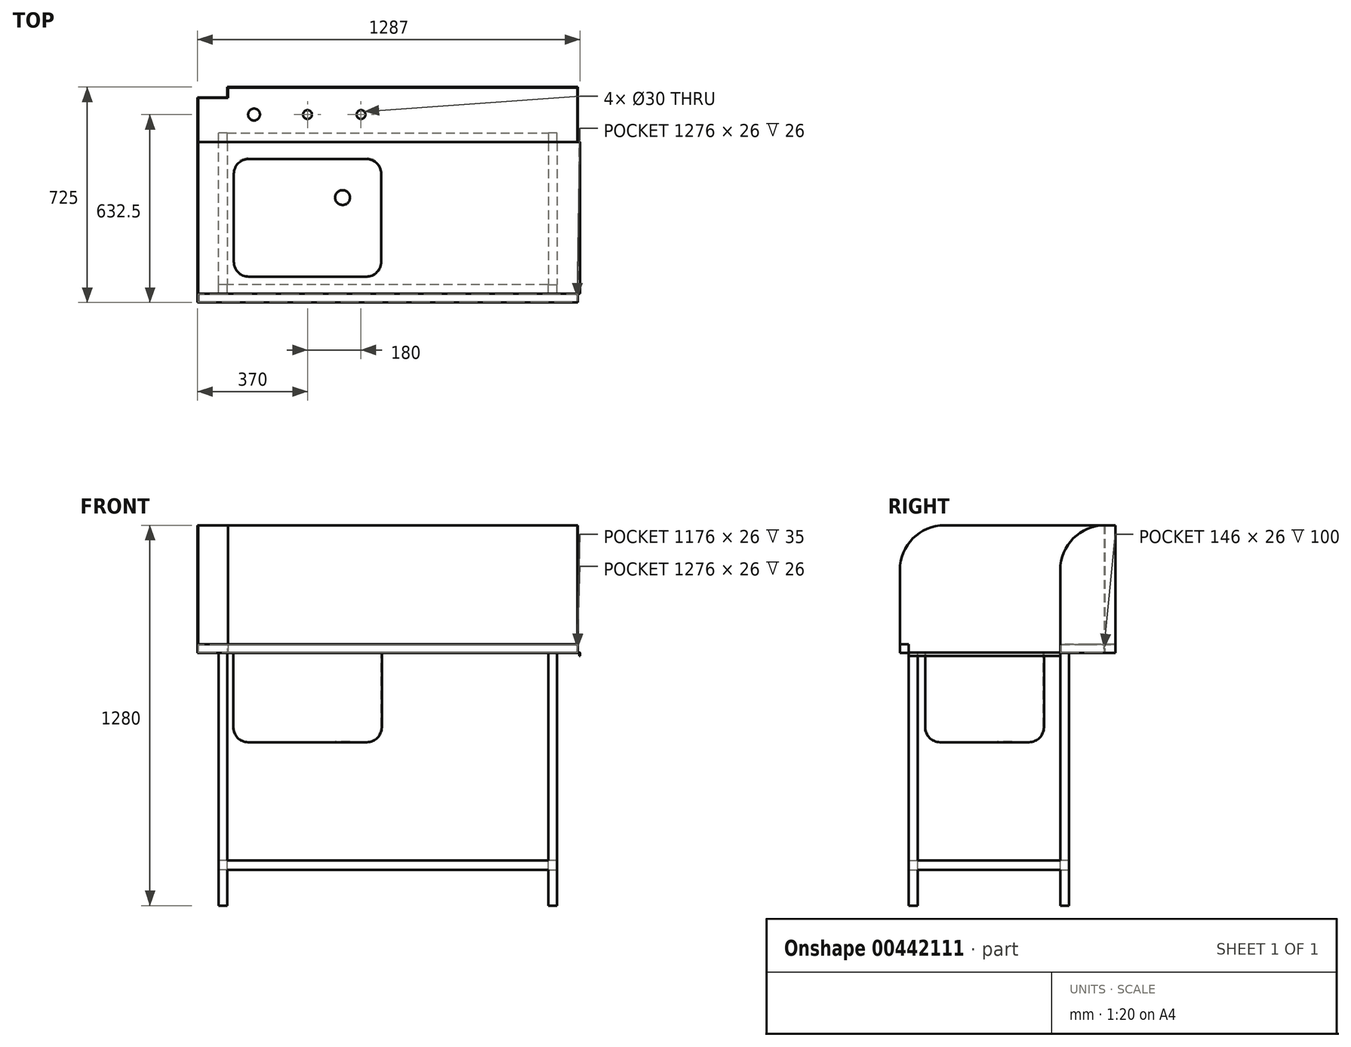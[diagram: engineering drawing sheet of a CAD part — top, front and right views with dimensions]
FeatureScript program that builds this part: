
annotation { "Feature Type Name" : "Feature", "Feature Type Description" : "" }
export const myFeature = defineFeature(function(context is Context, id is Id, definition is map)
    precondition{}
    {
        {
            var Q0;
            Q0=qCreatedBy(makeId("Top.planeOp"),FACE);
            var sketch = newSketch(context, id + "F0", { "sketchPlane" : qUnion([Q0])});
            skLineSegment(sketch, "E0", {"start": v(0, 0) * mm, "end": v(1280, 0) * mm});
            skLineSegment(sketch, "E1", {"start": v(1280, 0) * mm, "end": v(1280, 725) * mm});
            skLineSegment(sketch, "E2", {"start": v(1280, 725) * mm, "end": v(100, 725) * mm});
            skLineSegment(sketch, "E3", {"start": v(100, 725) * mm, "end": v(100, 690) * mm});
            skLineSegment(sketch, "E4", {"start": v(100, 690) * mm, "end": v(0, 690) * mm});
            skLineSegment(sketch, "E5", {"start": v(0, 690) * mm, "end": v(0, 0) * mm});
            skSolve(sketch);
        }
        {
            var Q0;
            Q0 = qSketchRegion(id + "F0", true);
            extrude(context, id + "F1", {"entities" : qUnion([Q0]), "depth" : 30 * mm});
        }
        {
            var Q0;
            Q0=makeQuery(id+"F1.opExtrude","CAP_FACE",FACE,{"disambiguationData":[OSD([sQuery(id+"F0.wireOp",EDGE,"E0"),sQuery(id+"F0.wireOp",EDGE,"E1"),sQuery(id+"F0.wireOp",EDGE,"E2"),sQuery(id+"F0.wireOp",EDGE,"E3"),sQuery(id+"F0.wireOp",EDGE,"E4"),sQuery(id+"F0.wireOp",EDGE,"E5")])],"isStart":false});
            var sketch = newSketch(context, id + "F2", { "sketchPlane" : qUnion([Q0])});
            skLineSegment(sketch, "E6.bottom", {"start": v(2, 30) * mm, "end": v(1280, 30) * mm});
            skLineSegment(sketch, "E6.top", {"start": v(2, 540) * mm, "end": v(1280, 540) * mm});
            skLineSegment(sketch, "E6.left", {"start": v(2, 30) * mm, "end": v(2, 540) * mm});
            skLineSegment(sketch, "E6.right", {"start": v(1280, 30) * mm, "end": v(1280, 540) * mm});
            skSolve(sketch);
        }
        {
            var Q0;
            Q0 = qSketchRegion(id + "F2", true);
            extrude(context, id + "F3", {"entities" : qUnion([Q0]), "operationType" : NewBodyOperationType.REMOVE, "oppositeDirection" : true, "depth" : 28 * mm});
        }
        {
            var Q0;
            Q0=makeQuery(id+"F1.opExtrude","CAP_FACE",FACE,{"disambiguationData":[OSD([sQuery(id+"F0.wireOp",EDGE,"E0"),sQuery(id+"F0.wireOp",EDGE,"E1"),sQuery(id+"F0.wireOp",EDGE,"E2"),sQuery(id+"F0.wireOp",EDGE,"E3"),sQuery(id+"F0.wireOp",EDGE,"E4"),sQuery(id+"F0.wireOp",EDGE,"E5")])],"isStart":true});
            var sketch = newSketch(context, id + "F4", { "sketchPlane" : qUnion([Q0])});
            skLineSegment(sketch, "E7.bottom", {"start": v(120, -85) * mm, "end": v(620, -85) * mm});
            skLineSegment(sketch, "E7.top", {"start": v(120, -485) * mm, "end": v(620, -485) * mm});
            skLineSegment(sketch, "E7.left", {"start": v(120, -85) * mm, "end": v(120, -485) * mm});
            skLineSegment(sketch, "E7.right", {"start": v(620, -85) * mm, "end": v(620, -485) * mm});
            skSolve(sketch);
        }
        {
            var Q0;
            Q0 = qSketchRegion(id + "F4", true);
            extrude(context, id + "F5", {"entities" : qUnion([Q0]), "operationType" : NewBodyOperationType.ADD, "depth" : 300 * mm});
        }
        {
            var Q0;
            Q0=makeQuery(id+"F3.boolean.opBoolean","COPY",FACE,{"derivedFrom":makeQuery(id+"F3.opExtrude","CAP_FACE",FACE,{"disambiguationData":[OSD([sQuery(id+"F2.wireOp",EDGE,"E6.bottom"),sQuery(id+"F2.wireOp",EDGE,"E6.top"),sQuery(id+"F2.wireOp",EDGE,"E6.left"),sQuery(id+"F2.wireOp",EDGE,"E6.right")])],"isStart":false})});
            shell(context, id + "F6", {"entities" : qUnion([Q0]), "thickness" : 2 * mm});
        }
        {
            var Q0;
            Q0=makeQuery(id+"F6.opShell","OFFSET_EDGE",EDGE,{"disambiguationData":[OSD([sQuery(id+"F4.wireOp",EDGE,"E7.top"),sQuery(id+"F4.wireOp",EDGE,"E7.left")])]});
            var Q1;
            Q1=makeQuery(id+"F6.opShell","OFFSET_EDGE",EDGE,{"disambiguationData":[OSD([sQuery(id+"F4.wireOp",EDGE,"E7.top"),sQuery(id+"F4.wireOp",EDGE,"E7.right")])]});
            var Q2;
            Q2=makeQuery(id+"F6.opShell","OFFSET_EDGE",EDGE,{"disambiguationData":[OSD([sQuery(id+"F4.wireOp",EDGE,"E7.bottom"),sQuery(id+"F4.wireOp",EDGE,"E7.left")])]});
            var Q3;
            Q3=makeQuery(id+"F6.opShell","OFFSET_EDGE",EDGE,{"disambiguationData":[OSD([sQuery(id+"F4.wireOp",EDGE,"E7.bottom"),sQuery(id+"F4.wireOp",EDGE,"E7.right")])]});
            var Q4;
            {var subQ0=sQuery(id+"F4.wireOp",EDGE,"E7.right");Q4=makeQuery(id+"F6.opShell","OFFSET_EDGE",EDGE,{"disambiguationData":[OSD([subQ0]),TDD([makeQuery(id+"F5.opExtrude","CAP_EDGE",EDGE,{"disambiguationData":[OSD([subQ0])],"isStart":false})])]});}
            var Q5;
            {var subQ0=sQuery(id+"F4.wireOp",EDGE,"E7.top");Q5=makeQuery(id+"F6.opShell","OFFSET_EDGE",EDGE,{"disambiguationData":[OSD([subQ0]),TDD([makeQuery(id+"F5.opExtrude","CAP_EDGE",EDGE,{"disambiguationData":[OSD([subQ0])],"isStart":false})])]});}
            var Q6;
            {var subQ0=sQuery(id+"F4.wireOp",EDGE,"E7.left");Q6=makeQuery(id+"F6.opShell","OFFSET_EDGE",EDGE,{"disambiguationData":[OSD([subQ0]),TDD([makeQuery(id+"F5.opExtrude","CAP_EDGE",EDGE,{"disambiguationData":[OSD([subQ0])],"isStart":false})])]});}
            var Q7;
            {var subQ0=sQuery(id+"F4.wireOp",EDGE,"E7.bottom");Q7=makeQuery(id+"F6.opShell","OFFSET_EDGE",EDGE,{"disambiguationData":[OSD([subQ0]),TDD([makeQuery(id+"F5.opExtrude","CAP_EDGE",EDGE,{"disambiguationData":[OSD([subQ0])],"isStart":false})])]});}
            var Q8;
            Q8=makeQuery(id+"F5.opExtrude","SWEPT_EDGE",EDGE,{"disambiguationData":[OSD([sQuery(id+"F4.wireOp",EDGE,"E7.bottom"),sQuery(id+"F4.wireOp",EDGE,"E7.left")])]});
            var Q9;
            Q9=makeQuery(id+"F5.opExtrude","CAP_EDGE",EDGE,{"disambiguationData":[OSD([sQuery(id+"F4.wireOp",EDGE,"E7.bottom")])],"isStart":false});
            var Q10;
            Q10=makeQuery(id+"F5.opExtrude","SWEPT_EDGE",EDGE,{"disambiguationData":[OSD([sQuery(id+"F4.wireOp",EDGE,"E7.bottom"),sQuery(id+"F4.wireOp",EDGE,"E7.right")])]});
            var Q11;
            Q11=makeQuery(id+"F5.opExtrude","CAP_EDGE",EDGE,{"disambiguationData":[OSD([sQuery(id+"F4.wireOp",EDGE,"E7.right")])],"isStart":false});
            var Q12;
            Q12=makeQuery(id+"F5.opExtrude","SWEPT_EDGE",EDGE,{"disambiguationData":[OSD([sQuery(id+"F4.wireOp",EDGE,"E7.top"),sQuery(id+"F4.wireOp",EDGE,"E7.right")])]});
            var Q13;
            Q13=makeQuery(id+"F5.opExtrude","CAP_EDGE",EDGE,{"disambiguationData":[OSD([sQuery(id+"F4.wireOp",EDGE,"E7.top")])],"isStart":false});
            var Q14;
            Q14=makeQuery(id+"F5.opExtrude","SWEPT_EDGE",EDGE,{"disambiguationData":[OSD([sQuery(id+"F4.wireOp",EDGE,"E7.top"),sQuery(id+"F4.wireOp",EDGE,"E7.left")])]});
            var Q15;
            Q15=makeQuery(id+"F5.opExtrude","CAP_EDGE",EDGE,{"disambiguationData":[OSD([sQuery(id+"F4.wireOp",EDGE,"E7.left")])],"isStart":false});
            fillet(context, id + "F7", {"entities" : qUnion([Q0, Q1, Q2, Q3, Q4, Q5, Q6, Q7, Q8, Q9, Q10, Q11, Q12, Q13, Q14, Q15]), "radius" : 50 * mm, "tangentPropagation" : true, "allowEdgeOverflow" : false});
        }
        {
            var Q0;
            Q0=makeQuery(id+"F6.opShell","OFFSET_FACE",FACE,{"disambiguationData":[OSD([sQuery(id+"F4.wireOp",EDGE,"E7.bottom"),sQuery(id+"F4.wireOp",EDGE,"E7.top"),sQuery(id+"F4.wireOp",EDGE,"E7.left"),sQuery(id+"F4.wireOp",EDGE,"E7.right")])]});
            var sketch = newSketch(context, id + "F8", { "sketchPlane" : qUnion([Q0])});
            skCircle(sketch, "E8", {"center": v(488, 353) * mm, "radius": 25 * mm});
            skSolve(sketch);
        }
        {
            var Q0;
            Q0 = qSketchRegion(id + "F8", true);
            extrude(context, id + "F9", {"entities" : qUnion([Q0]), "operationType" : NewBodyOperationType.REMOVE, "endBound" : BoundingType.UP_TO_NEXT, "oppositeDirection" : true, "depth" : 25 * mm});
        }
        {
            var Q0;
            Q0=makeQuery(id+"F1.opExtrude","CAP_FACE",FACE,{"disambiguationData":[OSD([sQuery(id+"F0.wireOp",EDGE,"E0"),sQuery(id+"F0.wireOp",EDGE,"E1"),sQuery(id+"F0.wireOp",EDGE,"E2"),sQuery(id+"F0.wireOp",EDGE,"E3"),sQuery(id+"F0.wireOp",EDGE,"E4"),sQuery(id+"F0.wireOp",EDGE,"E5")])],"isStart":false});
            var sketch = newSketch(context, id + "F10", { "sketchPlane" : qUnion([Q0])});
            skCircle(sketch, "E9", {"center": v(550, 632.5) * mm, "radius": 15 * mm});
            skCircle(sketch, "E10", {"center": v(370, 632.5) * mm, "radius": 15 * mm});
            skCircle(sketch, "E11", {"center": v(190, 632.5) * mm, "radius": 20 * mm});
            skSolve(sketch);
        }
        {
            var Q0;
            Q0 = qSketchRegion(id + "F10", true);
            var Q1;
            Q1=makeQuery(id+"F1.opExtrude","CAP_FACE",FACE,{"disambiguationData":[OSD([sQuery(id+"F0.wireOp",EDGE,"E0"),sQuery(id+"F0.wireOp",EDGE,"E1"),sQuery(id+"F0.wireOp",EDGE,"E2"),sQuery(id+"F0.wireOp",EDGE,"E3"),sQuery(id+"F0.wireOp",EDGE,"E4"),sQuery(id+"F0.wireOp",EDGE,"E5")])],"isStart":true});
            extrude(context, id + "F11", {"entities" : qUnion([Q0]), "operationType" : NewBodyOperationType.REMOVE, "endBound" : BoundingType.UP_TO_SURFACE, "oppositeDirection" : true, "endBoundEntityFace" : qUnion([Q1]), "depth" : 25 * mm});
        }
        {
            var Q0;
            Q0=makeQuery(id+"F1.opExtrude","SWEPT_FACE",FACE,{"disambiguationData":[OSD([sQuery(id+"F0.wireOp",EDGE,"E1")])]});
            var sketch = newSketch(context, id + "F12", { "sketchPlane" : qUnion([Q0])});
            skLineSegment(sketch, "E12.bottom", {"start": v(30, 2) * mm, "end": v(540, 2) * mm});
            skLineSegment(sketch, "E12.top", {"start": v(30, 0) * mm, "end": v(540, 0) * mm});
            skLineSegment(sketch, "E12.left", {"start": v(30, 2) * mm, "end": v(30, 0) * mm});
            skLineSegment(sketch, "E12.right", {"start": v(540, 2) * mm, "end": v(540, 0) * mm});
            skSolve(sketch);
        }
        {
            var Q0;
            Q0 = qSketchRegion(id + "F12", true);
            extrude(context, id + "F13", {"entities" : qUnion([Q0]), "operationType" : NewBodyOperationType.ADD, "depth" : 5 * mm});
        }
        {
            var Q0;
            Q0=makeQuery(id+"F13.opExtrude","CAP_FACE",FACE,{"disambiguationData":[OSD([sQuery(id+"F12.wireOp",EDGE,"E12.bottom"),sQuery(id+"F12.wireOp",EDGE,"E12.top"),sQuery(id+"F12.wireOp",EDGE,"E12.left"),sQuery(id+"F12.wireOp",EDGE,"E12.right")])],"isStart":false});
            var sketch = newSketch(context, id + "F14", { "sketchPlane" : qUnion([Q0])});
            skSolve(sketch);
        }
        {
            var Q0;
            Q0=makeQuery(id+"F14.imprint","IMPRINT",FACE,{"disambiguationData":[TD([[makeQuery(id+"F14.imprint","IMPRINT",EDGE,{"derivedFrom":makeQuery(id+"F13.opExtrude","CAP_EDGE",EDGE,{"disambiguationData":[OSD([sQuery(id+"F12.wireOp",EDGE,"E12.bottom")])],"isStart":false})}),-1.0]])]});
            var Q1;
            Q1=makeQuery(id+"F13.opExtrude","CAP_EDGE",EDGE,{"disambiguationData":[OSD([sQuery(id+"F12.wireOp",EDGE,"E12.top")])],"isStart":false});
            revolve(context, id + "F15", {"operationType" : NewBodyOperationType.ADD, "entities" : qUnion([Q0]), "axis" : qUnion([Q1]), "revolveType" : RevolveType.ONE_DIRECTION, "angle" : 90 * degree});
        }
        {
            var Q0;
            {var subQ0=sQuery(id+"F12.wireOp",EDGE,"E12.top");Q0=makeQuery(id+"F15.boolean.opBoolean","MERGE",FACE,{"derivedFrom":[makeQuery(id+"F13.boolean.opBoolean","MERGE",FACE,{"derivedFrom":[makeQuery(id+"F1.opExtrude","CAP_FACE",FACE,{"disambiguationData":[OSD([sQuery(id+"F0.wireOp",EDGE,"E0"),sQuery(id+"F0.wireOp",EDGE,"E1"),sQuery(id+"F0.wireOp",EDGE,"E2"),sQuery(id+"F0.wireOp",EDGE,"E3"),sQuery(id+"F0.wireOp",EDGE,"E4"),sQuery(id+"F0.wireOp",EDGE,"E5")])],"isStart":true}),makeQuery(id+"F13.opExtrude","SWEPT_FACE",FACE,{"disambiguationData":[OSD([subQ0])]})]}),makeQuery(id+"F15.opRevolve","CAP_FACE",FACE,{"disambiguationData":[OSD([sQuery(id+"F12.wireOp",EDGE,"E12.bottom"),subQ0,sQuery(id+"F12.wireOp",EDGE,"E12.left"),sQuery(id+"F12.wireOp",EDGE,"E12.right")])],"isStart":false})]});}
            var sketch = newSketch(context, id + "F16", { "sketchPlane" : qUnion([Q0])});
            skLineSegment(sketch, "E13.bottom", {"start": v(1287, -30) * mm, "end": v(1285, -30) * mm});
            skLineSegment(sketch, "E13.top", {"start": v(1287, -540) * mm, "end": v(1285, -540) * mm});
            skLineSegment(sketch, "E13.left", {"start": v(1287, -30) * mm, "end": v(1287, -540) * mm});
            skLineSegment(sketch, "E13.right", {"start": v(1285, -30) * mm, "end": v(1285, -540) * mm});
            skSolve(sketch);
        }
        {
            var Q0;
            Q0 = qSketchRegion(id + "F16", true);
            extrude(context, id + "F17", {"entities" : qUnion([Q0]), "operationType" : NewBodyOperationType.ADD, "depth" : 10 * mm});
        }
        {
            var Q0;
            Q0=makeQuery(id+"F1.opExtrude","CAP_FACE",FACE,{"disambiguationData":[OSD([sQuery(id+"F0.wireOp",EDGE,"E0"),sQuery(id+"F0.wireOp",EDGE,"E1"),sQuery(id+"F0.wireOp",EDGE,"E2"),sQuery(id+"F0.wireOp",EDGE,"E3"),sQuery(id+"F0.wireOp",EDGE,"E4"),sQuery(id+"F0.wireOp",EDGE,"E5")])],"isStart":false});
            var sketch = newSketch(context, id + "F18", { "sketchPlane" : qUnion([Q0])});
            skLineSegment(sketch, "E14", {"start": v(1280, 540) * mm, "end": v(1280, 725) * mm});
            skLineSegment(sketch, "E15", {"start": v(1280, 725) * mm, "end": v(100, 725) * mm});
            skLineSegment(sketch, "E16", {"start": v(100, 725) * mm, "end": v(100, 690) * mm});
            skLineSegment(sketch, "E17", {"start": v(100, 690) * mm, "end": v(0, 690) * mm});
            skLineSegment(sketch, "E18", {"start": v(0, 690) * mm, "end": v(0, 0) * mm});
            skLineSegment(sketch, "E19", {"start": v(0, 0) * mm, "end": v(2, 0) * mm});
            skLineSegment(sketch, "E20", {"start": v(2, 0) * mm, "end": v(2, 688) * mm});
            skLineSegment(sketch, "E21", {"start": v(2, 688) * mm, "end": v(102, 688) * mm});
            skLineSegment(sketch, "E22", {"start": v(102, 688) * mm, "end": v(102, 723) * mm});
            skLineSegment(sketch, "E23", {"start": v(102, 723) * mm, "end": v(1278, 723) * mm});
            skLineSegment(sketch, "E24", {"start": v(1278, 723) * mm, "end": v(1278, 540) * mm});
            skLineSegment(sketch, "E25", {"start": v(1278, 540) * mm, "end": v(1280, 540) * mm});
            skSolve(sketch);
        }
        {
            var Q0;
            Q0 = qSketchRegion(id + "F18", true);
            extrude(context, id + "F19", {"entities" : qUnion([Q0]), "operationType" : NewBodyOperationType.ADD, "depth" : 400 * mm});
        }
        {
            var Q0;
            Q0=makeQuery(id+"F19.opExtrude","CAP_EDGE",EDGE,{"disambiguationData":[OSD([sQuery(id+"F18.wireOp",EDGE,"E25")])],"isStart":false});
            var Q1;
            Q1=makeQuery(id+"F19.opExtrude","CAP_EDGE",EDGE,{"disambiguationData":[OSD([sQuery(id+"F18.wireOp",EDGE,"E19")])],"isStart":false});
            fillet(context, id + "F20", {"entities" : qUnion([Q0, Q1]), "radius" : 150 * mm, "tangentPropagation" : true, "allowEdgeOverflow" : false});
        }
        {
            var Q0;
            {var subQ0=sQuery(id+"F12.wireOp",EDGE,"E12.top");Q0=makeQuery(id+"F15.boolean.opBoolean","MERGE",FACE,{"derivedFrom":[makeQuery(id+"F13.boolean.opBoolean","MERGE",FACE,{"derivedFrom":[makeQuery(id+"F1.opExtrude","CAP_FACE",FACE,{"disambiguationData":[OSD([sQuery(id+"F0.wireOp",EDGE,"E0"),sQuery(id+"F0.wireOp",EDGE,"E1"),sQuery(id+"F0.wireOp",EDGE,"E2"),sQuery(id+"F0.wireOp",EDGE,"E3"),sQuery(id+"F0.wireOp",EDGE,"E4"),sQuery(id+"F0.wireOp",EDGE,"E5")])],"isStart":true}),makeQuery(id+"F13.opExtrude","SWEPT_FACE",FACE,{"disambiguationData":[OSD([subQ0])]})]}),makeQuery(id+"F15.opRevolve","CAP_FACE",FACE,{"disambiguationData":[OSD([sQuery(id+"F12.wireOp",EDGE,"E12.bottom"),subQ0,sQuery(id+"F12.wireOp",EDGE,"E12.left"),sQuery(id+"F12.wireOp",EDGE,"E12.right")])],"isStart":false})]});}
            var sketch = newSketch(context, id + "F21", { "sketchPlane" : qUnion([Q0])});
            skLineSegment(sketch, "E26.bottom", {"start": v(100, -30) * mm, "end": v(70, -30) * mm});
            skLineSegment(sketch, "E26.top", {"start": v(100, -60) * mm, "end": v(70, -60) * mm});
            skLineSegment(sketch, "E26.left", {"start": v(100, -30) * mm, "end": v(100, -60) * mm});
            skLineSegment(sketch, "E26.right", {"start": v(70, -30) * mm, "end": v(70, -60) * mm});
            skPoint(sketch, "E26.middle", {"position": v(85, -45) * mm});
            skLineSegment(sketch, "E27.bottom", {"start": v(1210, -30) * mm, "end": v(1180, -30) * mm});
            skLineSegment(sketch, "E27.top", {"start": v(1210, -60) * mm, "end": v(1180, -60) * mm});
            skLineSegment(sketch, "E27.left", {"start": v(1210, -30) * mm, "end": v(1210, -60) * mm});
            skLineSegment(sketch, "E27.right", {"start": v(1180, -30) * mm, "end": v(1180, -60) * mm});
            skPoint(sketch, "E27.middle", {"position": v(1195, -45) * mm});
            skPoint(sketch, "E27.middle.positionSnap0", {"position": v(70, -45) * mm});
            skPoint(sketch, "E27.centerSnap0", {"position": v(70, -45) * mm});
            skLineSegment(sketch, "E28.bottom", {"start": v(1210, -540) * mm, "end": v(1180, -540) * mm});
            skLineSegment(sketch, "E28.top", {"start": v(1210, -570) * mm, "end": v(1180, -570) * mm});
            skLineSegment(sketch, "E28.left", {"start": v(1210, -540) * mm, "end": v(1210, -570) * mm});
            skLineSegment(sketch, "E28.right", {"start": v(1180, -540) * mm, "end": v(1180, -570) * mm});
            skPoint(sketch, "E28.middle", {"position": v(1195, -555) * mm});
            skLineSegment(sketch, "E29.bottom", {"start": v(100, -540) * mm, "end": v(70, -540) * mm});
            skLineSegment(sketch, "E29.top", {"start": v(100, -570) * mm, "end": v(70, -570) * mm});
            skLineSegment(sketch, "E29.left", {"start": v(100, -540) * mm, "end": v(100, -570) * mm});
            skLineSegment(sketch, "E29.right", {"start": v(70, -540) * mm, "end": v(70, -570) * mm});
            skPoint(sketch, "E29.middle", {"position": v(85, -555) * mm});
            skPoint(sketch, "E29.middle.positionSnap0", {"position": v(1180, -555) * mm});
            skPoint(sketch, "E29.centerSnap0", {"position": v(1180, -555) * mm});
            skSolve(sketch);
        }
        {
            var Q0;
            Q0 = qSketchRegion(id + "F21", true);
            extrude(context, id + "F22", {"entities" : qUnion([Q0]), "operationType" : NewBodyOperationType.ADD, "depth" : 850 * mm});
        }
        {
            var Q0;
            Q0=makeQuery(id+"F22.opExtrude","SWEPT_FACE",FACE,{"disambiguationData":[OSD([sQuery(id+"F21.wireOp",EDGE,"E26.left")])]});
            var sketch = newSketch(context, id + "F23", { "sketchPlane" : qUnion([Q0])});
            skLineSegment(sketch, "E30.bottom", {"start": v(30, -730) * mm, "end": v(60, -730) * mm});
            skLineSegment(sketch, "E30.top", {"start": v(30, -700) * mm, "end": v(60, -700) * mm});
            skLineSegment(sketch, "E30.left", {"start": v(30, -730) * mm, "end": v(30, -700) * mm});
            skLineSegment(sketch, "E30.right", {"start": v(60, -730) * mm, "end": v(60, -700) * mm});
            skLineSegment(sketch, "E31.bottom", {"start": v(540, -700) * mm, "end": v(570, -700) * mm});
            skLineSegment(sketch, "E31.top", {"start": v(540, -730) * mm, "end": v(570, -730) * mm});
            skLineSegment(sketch, "E31.left", {"start": v(540, -700) * mm, "end": v(540, -730) * mm});
            skLineSegment(sketch, "E31.right", {"start": v(570, -700) * mm, "end": v(570, -730) * mm});
            skSolve(sketch);
        }
        {
            var Q0;
            Q0 = qSketchRegion(id + "F23", true);
            extrude(context, id + "F24", {"entities" : qUnion([Q0]), "operationType" : NewBodyOperationType.ADD, "endBound" : BoundingType.UP_TO_NEXT, "depth" : 25 * mm});
        }
        {
            var Q0;
            Q0=makeQuery(id+"F24.boolean.opBoolean","MERGE",FACE,{"derivedFrom":[makeQuery(id+"F22.opExtrude","SWEPT_FACE",FACE,{"disambiguationData":[OSD([sQuery(id+"F21.wireOp",EDGE,"E26.top")])]}),makeQuery(id+"F22.opExtrude","SWEPT_FACE",FACE,{"disambiguationData":[OSD([sQuery(id+"F21.wireOp",EDGE,"E27.top")])]}),makeQuery(id+"F24.opExtrude","SWEPT_FACE",FACE,{"disambiguationData":[OSD([sQuery(id+"F23.wireOp",EDGE,"E30.right")])]})]});
            var sketch = newSketch(context, id + "F25", { "sketchPlane" : qUnion([Q0])});
            skLineSegment(sketch, "E32.bottom", {"start": v(-1180, -730) * mm, "end": v(-1210, -730) * mm});
            skLineSegment(sketch, "E32.top", {"start": v(-1180, -700) * mm, "end": v(-1210, -700) * mm});
            skLineSegment(sketch, "E32.left", {"start": v(-1180, -730) * mm, "end": v(-1180, -700) * mm});
            skLineSegment(sketch, "E32.right", {"start": v(-1210, -730) * mm, "end": v(-1210, -700) * mm});
            skLineSegment(sketch, "E33.bottom", {"start": v(-100, -730) * mm, "end": v(-70, -730) * mm});
            skLineSegment(sketch, "E33.top", {"start": v(-100, -700) * mm, "end": v(-70, -700) * mm});
            skLineSegment(sketch, "E33.left", {"start": v(-100, -730) * mm, "end": v(-100, -700) * mm});
            skLineSegment(sketch, "E33.right", {"start": v(-70, -730) * mm, "end": v(-70, -700) * mm});
            skSolve(sketch);
        }
        {
            var Q0;
            Q0 = qSketchRegion(id + "F25", true);
            extrude(context, id + "F26", {"entities" : qUnion([Q0]), "operationType" : NewBodyOperationType.ADD, "endBound" : BoundingType.UP_TO_NEXT, "depth" : 25 * mm});
        }
        {
            var Q0;
            Q0=makeQuery(id+"F24.opExtrude","SWEPT_FACE",FACE,{"disambiguationData":[OSD([sQuery(id+"F23.wireOp",EDGE,"E30.top")])]});
            var sketch = newSketch(context, id + "F27", { "sketchPlane" : qUnion([Q0])});
            skLineSegment(sketch, "E34", {"start": v(100, 30) * mm, "end": v(100, 60) * mm});
            skLineSegment(sketch, "E35", {"start": v(100, 60) * mm, "end": v(70, 60) * mm});
            skLineSegment(sketch, "E36", {"start": v(70, 60) * mm, "end": v(70, 540) * mm});
            skLineSegment(sketch, "E37", {"start": v(70, 540) * mm, "end": v(100, 540) * mm});
            skLineSegment(sketch, "E38", {"start": v(100, 540) * mm, "end": v(100, 570) * mm});
            skLineSegment(sketch, "E39", {"start": v(100, 570) * mm, "end": v(1180, 570) * mm});
            skLineSegment(sketch, "E40", {"start": v(1180, 570) * mm, "end": v(1180, 540) * mm});
            skLineSegment(sketch, "E41", {"start": v(1180, 540) * mm, "end": v(1210, 540) * mm});
            skLineSegment(sketch, "E42", {"start": v(1210, 540) * mm, "end": v(1210, 60) * mm});
            skLineSegment(sketch, "E43", {"start": v(1210, 60) * mm, "end": v(1180, 60) * mm});
            skLineSegment(sketch, "E44", {"start": v(1180, 60) * mm, "end": v(1180, 30) * mm});
            skLineSegment(sketch, "E45", {"start": v(1180, 30) * mm, "end": v(100, 30) * mm});
            skSolve(sketch);
        }
        {
            var Q0;
            Q0 = qSketchRegion(id + "F27", true);
            extrude(context, id + "F28", {"entities" : qUnion([Q0]), "operationType" : NewBodyOperationType.ADD, "depth" : 2 * mm});
        }
    });
